# Revit family: RET_TP_RFA
name_source: partatom
category: Data Devices
revit_build: Autodesk Revit 2017 (Build: 20161205_1400(x64)
units: mm (PartAtom-declared; Revit-internal decimal feet)

## family parameters
Cut with Voids When Loaded = No
Host = Face
Maintain Annotation Orientation = Yes
Part Type = Normal
Room Calculation Point = No
Round Connector Dimension = Use Diameter
Shared = No

## types (8) — shared parameters
Ball Pressure Test = 75 C
Control Polution Situation = Degree 2
Default Elevation = 1500 mm  [stored 4.92126 ft]
H_2 = 43 mm  [stored 0.141076 ft]
IP Rating = IP30
IfcExportAs = IfcElectricApplianceType
IfcExportType = Controller
L_2 = 43 mm  [stored 0.141076 ft]
Manufacturer = Danfoss
Operating Temperature Range = 0-40 C
R1 = 33 mm  [stored 0.108268 ft]
R2 = 185 mm  [stored 0.606955 ft]
W3 = 1 mm  [stored 0.00328084 ft]

## per-type parameters (varying)
| type | Button_H | Description | Fault Indication | H1_2 | L1_2 | LCD backlight | Maximum Range | Model | Model Type | Operating Frequency | Output | Power Supply RT | RX1-S | Rated Impulse Voltage | Setting Temperature Range | Switch Rating | Switch Type | Type Comments | W | W1 | W2 | W4 | W5 | W6 |
| RET1001M_087N6460 | -2 mm  [stored -0.00656168 ft] | RET1001M |  | 39 mm  [stored 0.127953 ft] | 39 mm  [stored 0.127953 ft] |  | - | 087N6460 | Dial with LED indicator | 50/60 Hz | Volt Free | 230 VAC | No | 2.5 kV | 5-30 C | 3 A at 230VAC | 1 x SPDT Type 1B |  | 30 mm  [stored 0.0984252 ft] | 6 mm  [stored 0.019685 ft] | 6 mm  [stored 0.019685 ft] | 4 mm  [stored 0.0131234 ft] | 2 mm  [stored 0.00656168 ft] | 17 mm  [stored 0.0557743 ft] |
| RET2001B_087N6471 | 1 mm  [stored 0.00328084 ft] | RET2001B | Yes | 39 mm  [stored 0.127953 ft] | 39 mm  [stored 0.127953 ft] | Yes | - | 087N6471 | LCD backlit display with push buttons | - | Volt Free | 3 V DC Battery | No | 2.5 kV | 5-35 C | 3 A at 230VAC | 1 x SPDT Type 1B |  | 28 mm  [stored 0.0918635 ft] | 2 mm  [stored 0.00656168 ft] | 7 mm  [stored 0.0229659 ft] | 6 mm  [stored 0.019685 ft] | 2 mm  [stored 0.00656168 ft] | 13 mm |
| RET2001RF + RX1-S_087N7474 | 1 mm  [stored 0.00328084 ft] | RET2001RF + RX1-S | Yes | 39 mm  [stored 0.127953 ft] | 39 mm  [stored 0.127953 ft] | Yes | 30 m | 087N7474 | LCD backlit display with push buttons | - | RF 433.92 Mhz | 3 V DC Battery | Yes | 2.5 kV | 5-35 C | - | - |  | 28 mm  [stored 0.0918635 ft] | 2 mm  [stored 0.00656168 ft] | 7 mm  [stored 0.0229659 ft] | 6 mm  [stored 0.019685 ft] | 2 mm  [stored 0.00656168 ft] | 13 mm |
| TP5001B_087N7931 | 1 mm  [stored 0.00328084 ft] | TP5001B | Yes | 39 mm  [stored 0.127953 ft] | 39 mm  [stored 0.127953 ft] | Yes | - | 087N7931 | LCD backlit display with push buttons | - | Volt Free | 3 V DC Battery | No | 2.5 kV | 5-35 C | 3 A at 230VAC | 1 x SPDT Type 1B | Programmable Room Thermostats | 28 mm  [stored 0.0918635 ft] | 2 mm  [stored 0.00656168 ft] | 7 mm  [stored 0.0229659 ft] | 6 mm  [stored 0.019685 ft] | 2 mm  [stored 0.00656168 ft] | 13 mm |
| TP5001RF + RX1-S_087N7934 | 1 mm  [stored 0.00328084 ft] | TP5001RF + RX1-S | Yes | 39 mm  [stored 0.127953 ft] | 39 mm  [stored 0.127953 ft] | Yes | 30 m | 087N7934 | LCD backlit display with push buttons | - | RF 433.92 Mhz | 3 V DC Battery | Yes | 2.5 kV | 5-35 C | - | - | Programmable Room Thermostats | 28 mm  [stored 0.0918635 ft] | 2 mm  [stored 0.00656168 ft] | 7 mm  [stored 0.0229659 ft] | 6 mm  [stored 0.019685 ft] | 2 mm  [stored 0.00656168 ft] | 13 mm |
| RET2001M_087N6470 | 1 mm  [stored 0.00328084 ft] | RET2001M | Yes | 25 mm  [stored 0.082021 ft] | 25 mm  [stored 0.082021 ft] | Yes | - | 087N6470 | LCD backlit display with push buttons | 50/60 Hz | Volt Free | 230 VAC | No | 2.5 kV | 5-35 C | 3 A at 230VAC | 1 x SPDT Type 1B |  | 43 mm  [stored 0.141076 ft] | 2 mm  [stored 0.00656168 ft] | 6 mm  [stored 0.019685 ft] | 9 mm  [stored 0.0295276 ft] | 1 mm  [stored 0.00328084 ft] | 26 mm |
| TP5001M_087N7930 | 1 mm  [stored 0.00328084 ft] | TP5001M | Yes | 25 mm  [stored 0.082021 ft] | 25 mm  [stored 0.082021 ft] | Yes | - | 087N7930 | LCD backlit display with push buttons | 50/60 Hz | Volt Free | 230 VAC | No | 2.5 kV | 5-35 C | 3 A at 230VAC | 1 x SPDT Type 1B | Programmable Room Thermostats | 43 mm  [stored 0.141076 ft] | 2 mm  [stored 0.00656168 ft] | 6 mm  [stored 0.019685 ft] | 9 mm  [stored 0.0295276 ft] | 1 mm  [stored 0.00328084 ft] | 26 mm |
| RET2001OT_087N6475 | 1 mm  [stored 0.00328084 ft] | RET2001OT | Yes | 25 mm  [stored 0.082021 ft] | 25 mm  [stored 0.082021 ft] | Yes | - | 087N6475 | LCD backlit display with push buttons | 50/60 Hz | Data 24 VDC Bus | 24 VDC power line from boiler | No | - | 5-35 C | - | - |  | 43 mm  [stored 0.141076 ft] | 2 mm  [stored 0.00656168 ft] | 6 mm  [stored 0.019685 ft] | 9 mm  [stored 0.0295276 ft] | 1 mm  [stored 0.00328084 ft] | 26 mm |

note: [stored X ft] marks values corroborated as IEEE doubles in the binary element streams (Revit-internal decimal feet)

## geometry (parser evidence)
native form markers: Sweep x5
no freeform markers — native parametric forms only
